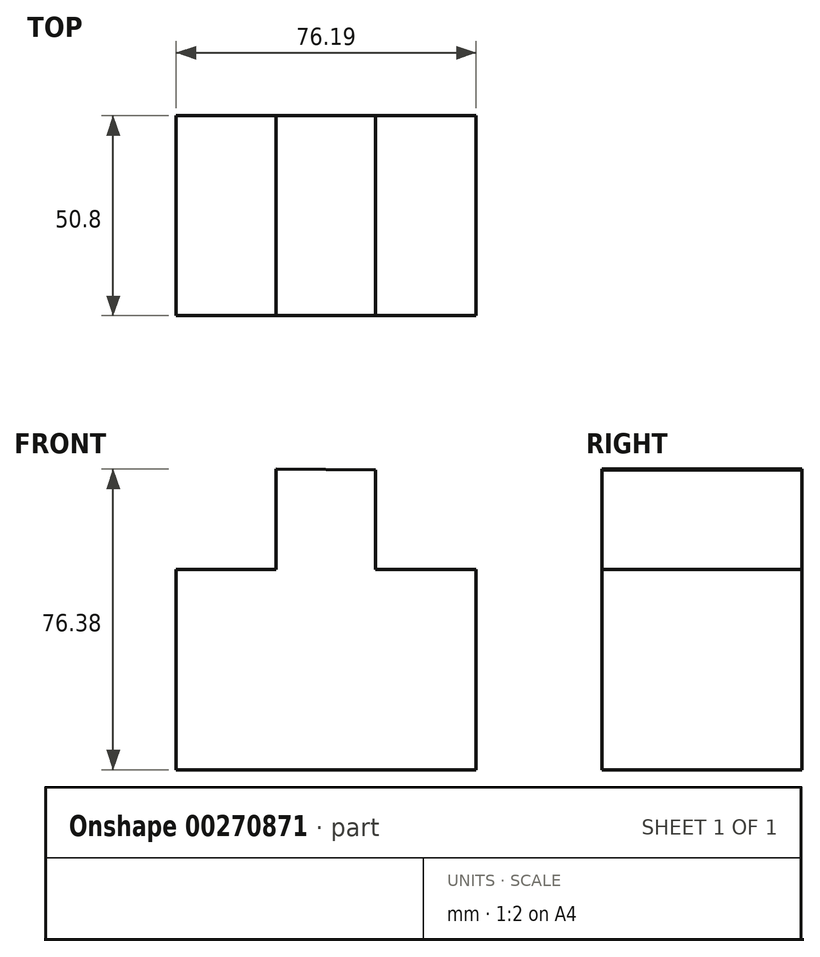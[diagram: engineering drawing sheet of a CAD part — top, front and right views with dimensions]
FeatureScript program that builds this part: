
annotation { "Feature Type Name" : "Feature", "Feature Type Description" : "" }
export const myFeature = defineFeature(function(context is Context, id is Id, definition is map)
    precondition{}
    {
        {
            var Q0;
            Q0=qCreatedBy(makeId("Front.planeOp"),FACE);
            var sketch = newSketch(context, id + "F0", { "sketchPlane" : qUnion([Q0])});
            skLineSegment(sketch, "E0", {"start": v(0, 0) * mm, "end": v(-76.2, 0) * mm});
            skPoint(sketch, "E1.end.orphan", {"position": v(0, 76.2) * mm});
            skPoint(sketch, "E2.end.orphan", {"position": v(-25.58, 76.2) * mm});
            skPoint(sketch, "E3.end.orphan", {"position": v(-76.2, 76.2) * mm});
            skLineSegment(sketch, "E4", {"start": v(-76.2, 0) * mm, "end": v(-76.2, 50.89) * mm});
            skLineSegment(sketch, "E5", {"start": v(-76.2, 50.89) * mm, "end": v(-50.87, 50.89) * mm});
            skLineSegment(sketch, "E6", {"start": v(-50.87, 50.89) * mm, "end": v(-50.87, 76.38) * mm});
            skLineSegment(sketch, "E7", {"start": v(-50.87, 76.38) * mm, "end": v(-25.58, 76.2) * mm});
            skLineSegment(sketch, "E8", {"start": v(-25.58, 50.89) * mm, "end": v(-25.58, 76.2) * mm});
            skLineSegment(sketch, "E9", {"start": v(-25.58, 50.89) * mm, "end": v(0, 50.89) * mm});
            skLineSegment(sketch, "E10", {"start": v(0, 50.89) * mm, "end": v(0, 0) * mm});
            skSolve(sketch);
        }
        {
            var Q0;
            Q0 = qSketchRegion(id + "F0", true);
            extrude(context, id + "F1", {"entities" : qUnion([Q0]), "depth" : 50.8 * mm});
        }
    });
